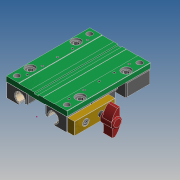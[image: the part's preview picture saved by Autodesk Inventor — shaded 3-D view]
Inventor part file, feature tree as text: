
AUTODESK INVENTOR PART (.ipt)
format: ipt  version: 2019 (Build 230136000, 136)  size: 6,966,784 bytes
history: native  units: mm
features: other x3, sketch x2, surface_op x1, hole x1, pattern_linear x1, extrude x1
ambient origin geometry x8: Origin, YZ Plane, XZ Plane, XY Plane, X Axis, Y Axis, Z Axis, Center Point
bodies: Solid1 (feature_tree)
feature tree (9):
  other  "WW_10_40_10_HKA_11"
  sketch  "Sketch2"  dims[d0=25.0mm d1=14.0mm d2=50.0mm]
  surface_op  "Stitch Surface1"
  hole  "Hole1"  [1 undecoded]
  pattern_linear  "Rectangular Pattern1"  Count1=5  [1 undecoded]
  extrude  "Extrusion1"  Depth=50.0mm
  sketch  "Sketch3"  dims[d6=2.459mm d7=6.0mm d8=4.0mm d9=2.0mm d10=90.0deg d11=8.8mm d12=20.594885mm d13=50.0mm d15=18.0mm d16=20.0mm d18=50.0mm d19=5.0mm d20=1.5mm d21=10.0mm d22=0.0mm]
  other  "Composite1"
  other  "Srf1"
note: 2 required parameter values undecoded (feature->parameter linkage not recoverable at this tier; creation-order binding heuristic only, values carry confidence <= 0.55)
